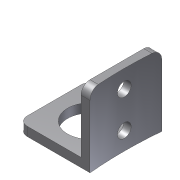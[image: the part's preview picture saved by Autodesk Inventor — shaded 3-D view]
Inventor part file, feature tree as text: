
AUTODESK INVENTOR PART (.ipt)
format: ipt  version: 2012 (Build 160160000, 160)  size: 129,536 bytes
history: native  units: in
note: dims shown in document units (in); Inventor stores cm internally (conversion verified against a paired STEP export)
features: extrude x4, sketch x4, fillet x1
ambient origin geometry x8: Origin, YZ Plane, XZ Plane, XY Plane, X Axis, Y Axis, Z Axis, Center Point
bodies: Solid1 (feature_tree)
feature tree (9):
  extrude  "Extrusion1"  Depth=1.0in
  extrude  "Extrusion2"  Depth=0.192in
  extrude  "Extrusion3"  Depth=0.5in
  fillet  "Fillet1"  Radius=0.5in
  extrude  "Extrusion4"  Depth=1.0in TaperAngle=0.0deg
  sketch  "Sketch1"  dims[d0=0.125in d1=1.0in]
  sketch  "Sketch2"  dims[d2=1.0in d3=0.0in d4=0.192in]
  sketch  "Sketch3"  dims[d5=0.192in d6=0.5in d7=0.5in]
  sketch  "Sketch4"  dims[d8=0.25in d9=1.0in d10=0.0in d11=0.5in d12=0.5in d13=0.625in d14=1.0in d15=0.0in d16=0.125in d17=5.5in d18=1.0in d19=0.0in]
